# Revit family: Showerhead-American_Standard-Town_Square_S-1660516_Series
name_source: partatom
category: Plumbing Fixtures
units: mm (PartAtom-declared; Revit-internal decimal feet)

## family parameters
Always vertical = No
Cut with Voids When Loaded = No
OmniClass Number = 23.45.05.14.17
OmniClass Title = Showers
Part Type = Normal
Room Calculation Point = No
Round Connector Dimension = Use Diameter
Shared = Yes
Work Plane-Based = Yes

## types (4) — shared parameters
ADA Compliant = Yes
Assembly Code = D2010710
CW Connection = No
CWFU = 3
Compliance Certifications = ASME A112.18.1, CSA B125.1
Default Elevation = 0"
Description = Town Square® S 6-1/4-Inch 2.5 gpm/9.5 L/min Fixed Showerhead
Flow Rate = 2.5 gpm (9.5 L/min)
HW Connection = No
HWFU = 3
Height = 2 11/16"
Length = 6 5/16"
Manufacturer = American Standard
Price = Prices may vary. Please consult Manufacturer Representative for most up-to-date price list.
Product Documentation Link = https://americanstandard.box.com
Product Page URL = https://www.americanstandard-us.com
Revised Date = 07/25/2022
Tempered Water Connection = Yes
Tempered Water Connection Diameter = 1/2"
URL = https://www.americanstandard-us.com
Vent Connection = No
WFU = 4
Warranty Information = One Year General Product Warranty
Waste Connection = No
Width = 6 5/16"

## per-type parameters (varying)
| type | Finish | Material |
| 1660.516.002 | Plastic-American Standard-002-Polished Chrome | Plastic-American Standard-002-Polished Chrome |
| 1660.516.295 | Plastic-American Standard-295-Brushed Nickel | Plastic-American Standard-295-Brushed Nickel |
| 1660.516.013 | Plastic-American Standard-013-Polished Nickel PVD | Plastic-American Standard-013-Polished Nickel PVD |
| 1660.516.278 | Plastic-American Standard-278-Legacy Bronze | Plastic-American Standard-278-Legacy Bronze |

note: column(s) folded — value = type name in every type: Model

## geometry (parser evidence)
native form markers: Sweep x2
no freeform markers — native parametric forms only
